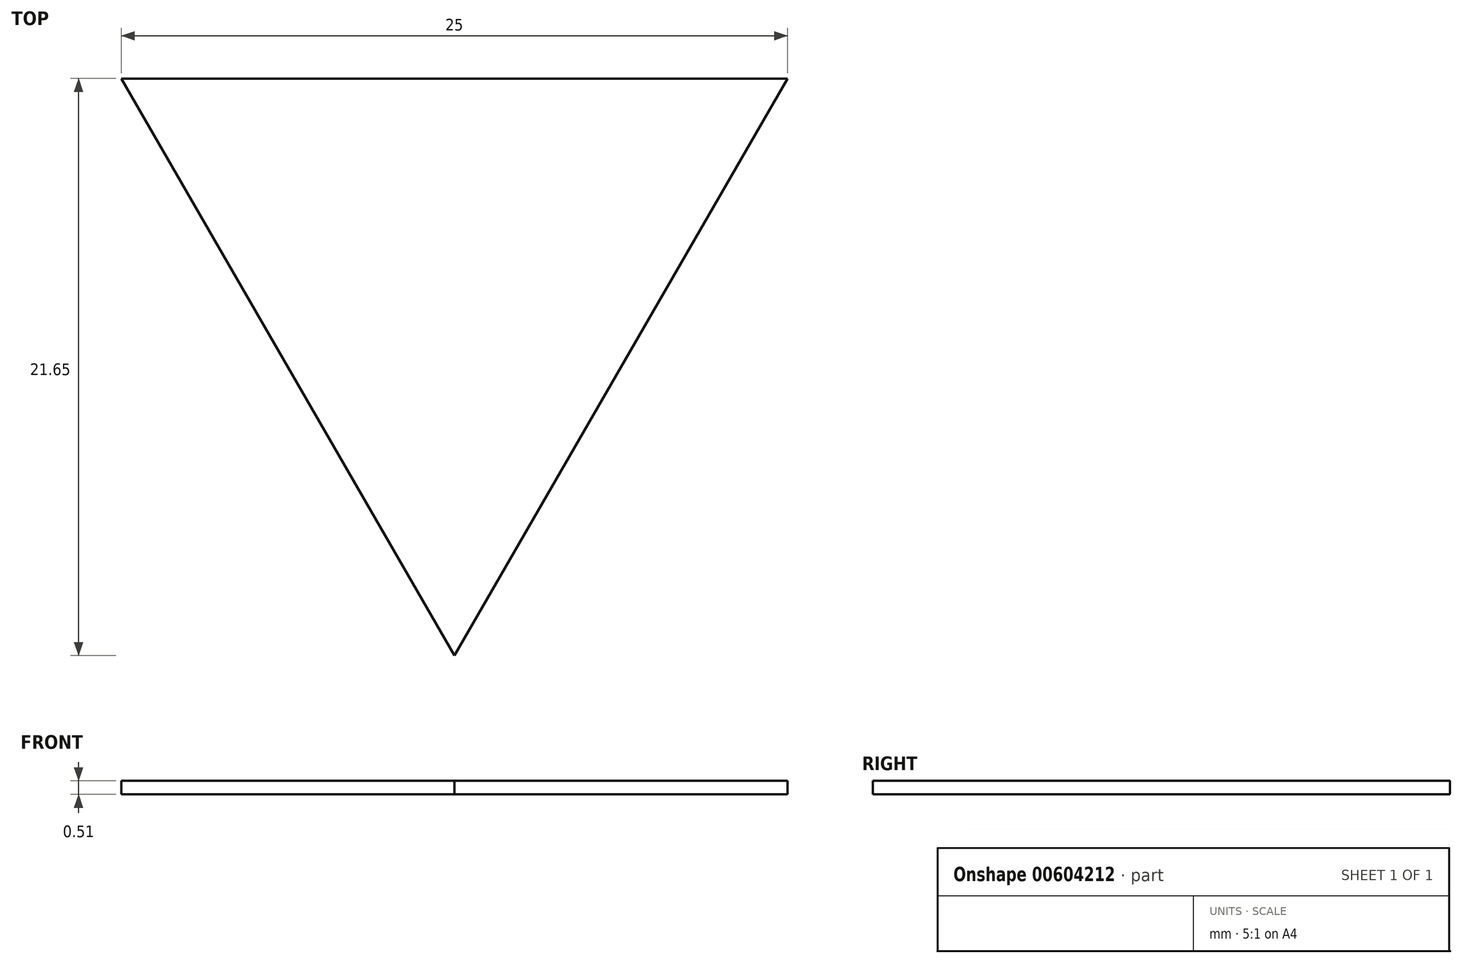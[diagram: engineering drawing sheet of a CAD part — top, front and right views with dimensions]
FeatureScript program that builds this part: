
annotation { "Feature Type Name" : "Feature", "Feature Type Description" : "" }
export const myFeature = defineFeature(function(context is Context, id is Id, definition is map)
    precondition{}
    {
        {
            var Q0;
            Q0=qCreatedBy(makeId("Top.planeOp"),FACE);
            var sketch = newSketch(context, id + "F0", { "sketchPlane" : qUnion([Q0])});
            skCircle(sketch, "E0.cCircle", {"center": v(0, 0) * mm, "radius": 7.22 * mm, "construction": true});
            skLineSegment(sketch, "E0.0", {"start": v(-12.5, 7.22) * mm, "end": v(12.5, 7.22) * mm});
            skLineSegment(sketch, "E0.1", {"start": v(12.5, 7.22) * mm, "end": v(0, -14.43) * mm});
            skLineSegment(sketch, "E0.2", {"start": v(0, -14.43) * mm, "end": v(-12.5, 7.22) * mm});
            skPoint(sketch, "E0.0.midPoint", {"position": v(0, 7.22) * mm});
            skSolve(sketch);
        }
        {
            var Q0;
            Q0 = qSketchRegion(id + "F0", true);
            extrude(context, id + "F1", {"entities" : qUnion([Q0]), "depth" : 0.5 * mm, "offsetDistance" : 25.4 * mm});
        }
    });
